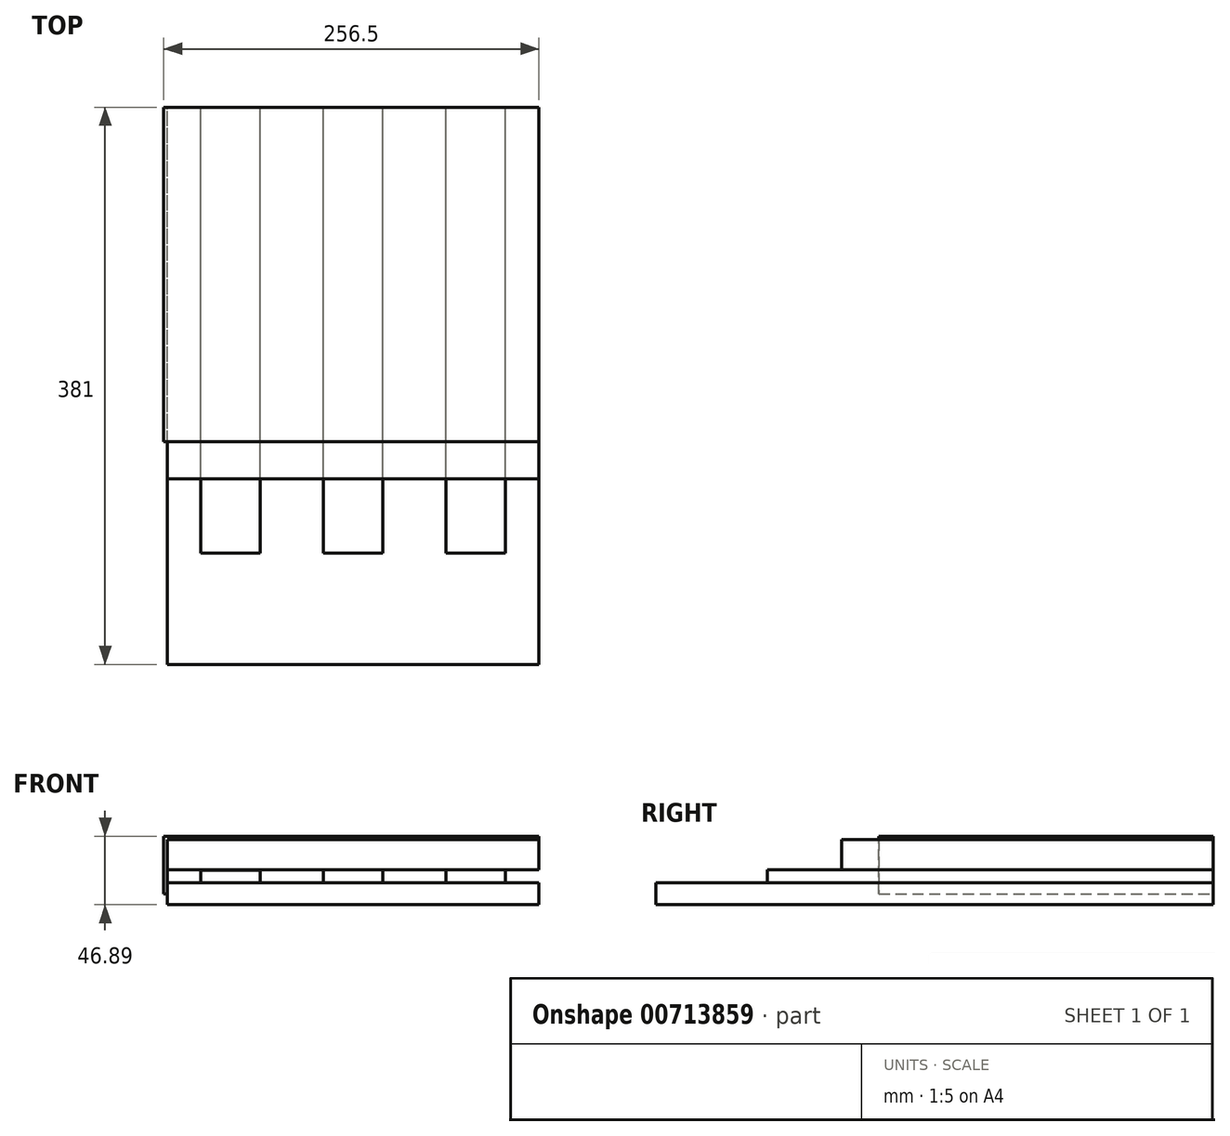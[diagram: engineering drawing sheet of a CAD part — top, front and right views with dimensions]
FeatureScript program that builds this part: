
annotation { "Feature Type Name" : "Feature", "Feature Type Description" : "" }
export const myFeature = defineFeature(function(context is Context, id is Id, definition is map)
    precondition{}
    {
        {
            var Q0;
            Q0=qCreatedBy(makeId("Front.planeOp"),FACE);
            var sketch = newSketch(context, id + "F0", { "sketchPlane" : qUnion([Q0])});
            skLineSegment(sketch, "E0.bottom", {"start": v(-156.07, 7.84) * mm, "end": v(97.93, 7.84) * mm});
            skLineSegment(sketch, "E0.top", {"start": v(-156.07, -7.12) * mm, "end": v(97.93, -7.12) * mm});
            skLineSegment(sketch, "E0.left", {"start": v(-156.07, 7.84) * mm, "end": v(-156.07, -7.12) * mm});
            skLineSegment(sketch, "E0.right", {"start": v(97.93, 7.84) * mm, "end": v(97.93, -7.12) * mm});
            skLineSegment(sketch, "E1.bottom", {"start": v(-156.07, 7.84) * mm, "end": v(-153.53, 7.84) * mm});
            skLineSegment(sketch, "E1.top", {"start": v(-156.07, 16.87) * mm, "end": v(-153.53, 16.87) * mm});
            skLineSegment(sketch, "E1.left", {"start": v(-156.07, 7.84) * mm, "end": v(-156.07, 16.87) * mm});
            skLineSegment(sketch, "E1.right", {"start": v(-153.53, 7.84) * mm, "end": v(-153.53, 16.87) * mm});
            skLineSegment(sketch, "E2.bottom", {"start": v(-72.25, 7.84) * mm, "end": v(-69.71, 7.84) * mm});
            skLineSegment(sketch, "E2.top", {"start": v(-72.25, 16.87) * mm, "end": v(-69.71, 16.87) * mm});
            skLineSegment(sketch, "E2.left", {"start": v(-72.25, 7.84) * mm, "end": v(-72.25, 16.87) * mm});
            skLineSegment(sketch, "E2.right", {"start": v(-69.71, 7.84) * mm, "end": v(-69.71, 16.87) * mm});
            skLineSegment(sketch, "E3.bottom", {"start": v(11.57, 7.84) * mm, "end": v(14.1, 7.84) * mm});
            skLineSegment(sketch, "E3.top", {"start": v(11.57, 16.87) * mm, "end": v(14.1, 16.87) * mm});
            skLineSegment(sketch, "E3.left", {"start": v(11.57, 7.84) * mm, "end": v(11.57, 16.87) * mm});
            skLineSegment(sketch, "E3.right", {"start": v(14.1, 7.84) * mm, "end": v(14.1, 16.87) * mm});
            skLineSegment(sketch, "E4.bottom", {"start": v(97.93, 7.84) * mm, "end": v(95.39, 7.84) * mm});
            skLineSegment(sketch, "E4.top", {"start": v(97.93, 16.87) * mm, "end": v(95.39, 16.87) * mm});
            skLineSegment(sketch, "E4.left", {"start": v(97.93, 7.84) * mm, "end": v(97.93, 16.87) * mm});
            skLineSegment(sketch, "E4.right", {"start": v(95.39, 7.84) * mm, "end": v(95.39, 16.87) * mm});
            skLineSegment(sketch, "E5", {"start": v(-133.21, 7.84) * mm, "end": v(-133.21, 16.6) * mm});
            skLineSegment(sketch, "E6", {"start": v(-133.21, 16.6) * mm, "end": v(-92.57, 16.6) * mm});
            skLineSegment(sketch, "E7", {"start": v(-92.57, 16.6) * mm, "end": v(-92.57, 7.84) * mm});
            skLineSegment(sketch, "E8", {"start": v(-49.4, 7.84) * mm, "end": v(-49.4, 16.9) * mm});
            skLineSegment(sketch, "E9", {"start": v(-49.4, 16.9) * mm, "end": v(-8.75, 16.9) * mm});
            skLineSegment(sketch, "E10", {"start": v(-8.75, 16.9) * mm, "end": v(-8.75, 7.84) * mm});
            skLineSegment(sketch, "E11", {"start": v(34.43, 7.84) * mm, "end": v(34.43, 16.89) * mm});
            skLineSegment(sketch, "E12", {"start": v(34.43, 16.89) * mm, "end": v(75.07, 16.89) * mm});
            skLineSegment(sketch, "E13", {"start": v(75.07, 16.89) * mm, "end": v(75.07, 7.84) * mm});
            skLineSegment(sketch, "E14", {"start": v(-156.07, 16.87) * mm, "end": v(97.93, 16.87) * mm, "construction": true});
            skLineSegment(sketch, "E15", {"start": v(-156.07, 16.87) * mm, "end": v(97.93, 16.87) * mm});
            skLineSegment(sketch, "E16", {"start": v(97.93, 16.87) * mm, "end": v(97.93, 37.34) * mm});
            skLineSegment(sketch, "E17", {"start": v(97.93, 37.34) * mm, "end": v(-156.07, 37.34) * mm});
            skLineSegment(sketch, "E18", {"start": v(-156.07, 37.34) * mm, "end": v(-156.07, 16.87) * mm});
            skLineSegment(sketch, "E19", {"start": v(-156.07, 0.36) * mm, "end": v(-158.56, 0.36) * mm});
            skLineSegment(sketch, "E20", {"start": v(-158.56, 0.36) * mm, "end": v(-158.56, 39.77) * mm});
            skLineSegment(sketch, "E21", {"start": v(-158.56, 39.77) * mm, "end": v(97.94, 39.77) * mm});
            skLineSegment(sketch, "E22", {"start": v(97.94, 39.77) * mm, "end": v(97.93, 37.34) * mm});
            skSolve(sketch);
        }
        {
            var Q0;
            {var subQ0=sQuery(id+"F0.wireOp",EDGE,"E0.top");Q0=makeQuery(id+"F0.imprint","IMPRINT",FACE,{"disambiguationData":[TD([[makeQuery(id+"F0.imprint","IMPRINT",EDGE,{"derivedFrom":subQ0}),1.0]])]});}
            var Q1;
            Q1=makeQuery(id+"F0.imprint","IMPRINT",FACE,{"disambiguationData":[TD([[makeQuery(id+"F0.imprint","IMPRINT",EDGE,{"derivedFrom":sQuery(id+"F0.wireOp",EDGE,"E1.bottom")}),1.0]])]});
            var Q2;
            Q2=makeQuery(id+"F0.imprint","IMPRINT",FACE,{"disambiguationData":[TD([[makeQuery(id+"F0.imprint","IMPRINT",EDGE,{"derivedFrom":sQuery(id+"F0.wireOp",EDGE,"E2.bottom")}),1.0]])]});
            var Q3;
            Q3=makeQuery(id+"F0.imprint","IMPRINT",FACE,{"disambiguationData":[TD([[makeQuery(id+"F0.imprint","IMPRINT",EDGE,{"derivedFrom":sQuery(id+"F0.wireOp",EDGE,"E3.bottom")}),1.0]])]});
            var Q4;
            Q4=makeQuery(id+"F0.imprint","IMPRINT",FACE,{"disambiguationData":[TD([[makeQuery(id+"F0.imprint","IMPRINT",EDGE,{"derivedFrom":sQuery(id+"F0.wireOp",EDGE,"E4.bottom")}),-1.0]])]});
            extrude(context, id + "F1", {"entities" : qUnion([Q0, Q1, Q2, Q3, Q4]), "depth" : 381 * mm});
        }
        {
            var Q0;
            {var subQ0=sQuery(id+"F0.wireOp",EDGE,"E5");Q0=makeQuery(id+"F0.imprint","IMPRINT",FACE,{"disambiguationData":[TD([[makeQuery(id+"F0.imprint","IMPRINT",EDGE,{"derivedFrom":subQ0}),-1.0]])]});}
            var Q1;
            {var subQ0=sQuery(id+"F0.wireOp",EDGE,"E8");var subQ1=sQuery(id+"F0.wireOp",EDGE,"E0.bottom");var subQ2=makeQuery(id+"F0.imprint","INTERSECT",VERTEX,{"derivedFrom":[subQ1,subQ0]});Q1=makeQuery(id+"F0.imprint","IMPRINT",FACE,{"disambiguationData":[TD([[makeQuery(id+"F0.imprint","IMPRINT",EDGE,{"disambiguationData":[TD([[subQ2,-1.0]])],"derivedFrom":subQ1}),1.0]])]});}
            var Q2;
            {var subQ0=sQuery(id+"F0.wireOp",EDGE,"E11");var subQ1=sQuery(id+"F0.wireOp",EDGE,"E0.bottom");var subQ2=makeQuery(id+"F0.imprint","INTERSECT",VERTEX,{"derivedFrom":[subQ1,subQ0]});Q2=makeQuery(id+"F0.imprint","IMPRINT",FACE,{"disambiguationData":[TD([[makeQuery(id+"F0.imprint","IMPRINT",EDGE,{"disambiguationData":[TD([[subQ2,-1.0]])],"derivedFrom":subQ1}),1.0]])]});}
            extrude(context, id + "F2", {"entities" : qUnion([Q0, Q1, Q2]), "depth" : 304.8 * mm});
        }
        {
            var Q0;
            {var subQ8=sQuery(id+"F0.wireOp",EDGE,"E9");Q0=makeQuery(id+"F0.imprint","IMPRINT",FACE,{"disambiguationData":[TD([[makeQuery(id+"F0.imprint","IMPRINT",EDGE,{"derivedFrom":subQ8}),1.0]])]});}
            extrude(context, id + "F3", {"entities" : qUnion([Q0]), "depth" : 254 * mm});
        }
        {
            var Q0;
            {var subQ0=sQuery(id+"F0.wireOp",EDGE,"E1.left");Q0=makeQuery(id+"F0.imprint","IMPRINT",FACE,{"disambiguationData":[TD([[makeQuery(id+"F0.imprint","IMPRINT",EDGE,{"derivedFrom":subQ0}),1.0]])]});}
            extrude(context, id + "F4", {"entities" : qUnion([Q0]), "depth" : 228.6 * mm});
        }
    });
